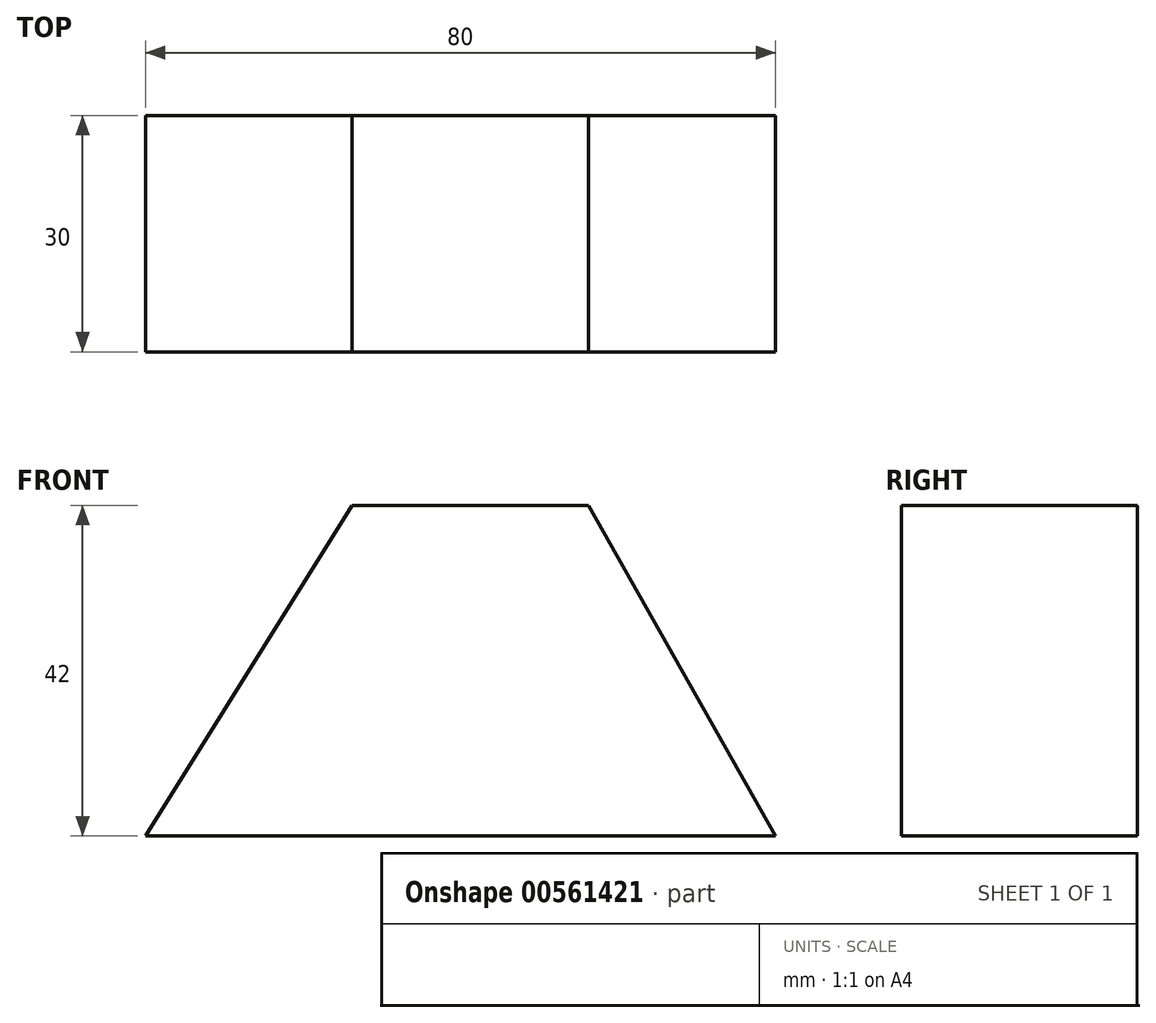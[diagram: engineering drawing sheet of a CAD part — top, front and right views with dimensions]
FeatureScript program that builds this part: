
annotation { "Feature Type Name" : "Feature", "Feature Type Description" : "" }
export const myFeature = defineFeature(function(context is Context, id is Id, definition is map)
    precondition{}
    {
        {
            var Q0;
            Q0=qCreatedBy(makeId("Front.planeOp"),FACE);
            var sketch = newSketch(context, id + "F0", { "sketchPlane" : qUnion([Q0])});
            skLineSegment(sketch, "E0", {"start": v(-35.42, -10.95) * mm, "end": v(-9.18, 31.05) * mm});
            skLineSegment(sketch, "E1", {"start": v(-9.18, 31.05) * mm, "end": v(20.82, 31.05) * mm});
            skLineSegment(sketch, "E2", {"start": v(20.82, 31.05) * mm, "end": v(44.58, -10.95) * mm});
            skLineSegment(sketch, "E3", {"start": v(44.58, -10.95) * mm, "end": v(-35.42, -10.95) * mm});
            skSolve(sketch);
        }
        {
            var Q0;
            Q0 = qSketchRegion(id + "F0", true);
            extrude(context, id + "F1", {"entities" : qUnion([Q0]), "depth" : 30 * mm, "offsetDistance" : 25 * mm});
        }
    });
